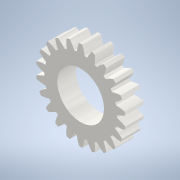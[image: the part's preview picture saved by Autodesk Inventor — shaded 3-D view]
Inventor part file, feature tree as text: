
AUTODESK INVENTOR PART (.ipt)
format: ipt  version: 2021 (Build 250183000, 183)  size: 239,616 bytes
history: native  units: mm (DEFAULTED — no unit token found)
features: plane x3, other x3, sketch x3, extrude x2
ambient origin geometry x8: Origin, YZ Plane, XZ Plane, XY Plane, X Axis, Y Axis, Z Axis, Center Point
bodies: Solid1 (feature_tree)
feature tree (11):
  extrude  "Extrusion1"  Depth=10.0mm TaperAngle=0.0deg
  plane  "Work Plane2"
  plane  "Work Plane8"
  plane  "Work Plane9"
  other  "Spur Gear"
  extrude  "Extrusion2"  Depth=10.0mm TaperAngle=0.0deg
  sketch  "Sketch1"  dims[d0=48.0mm d1=10.0mm d2=0.0mm]
  sketch  "Sketch2"  dims[d3=44.0mm d4=10.0mm d5=0.0mm]
  other  "Srf1"
  sketch  "Sketch3"  dims[d16=65.0mm d17=0.0mm d34=1.427997mm d39=0.0mm d41=0.0mm d43=65.0mm d46=65.0mm d47=0.0mm d48=0.0mm d49=25.0mm d50=10.0mm d51=0.0mm]
  other  "Pitch Diameter"
